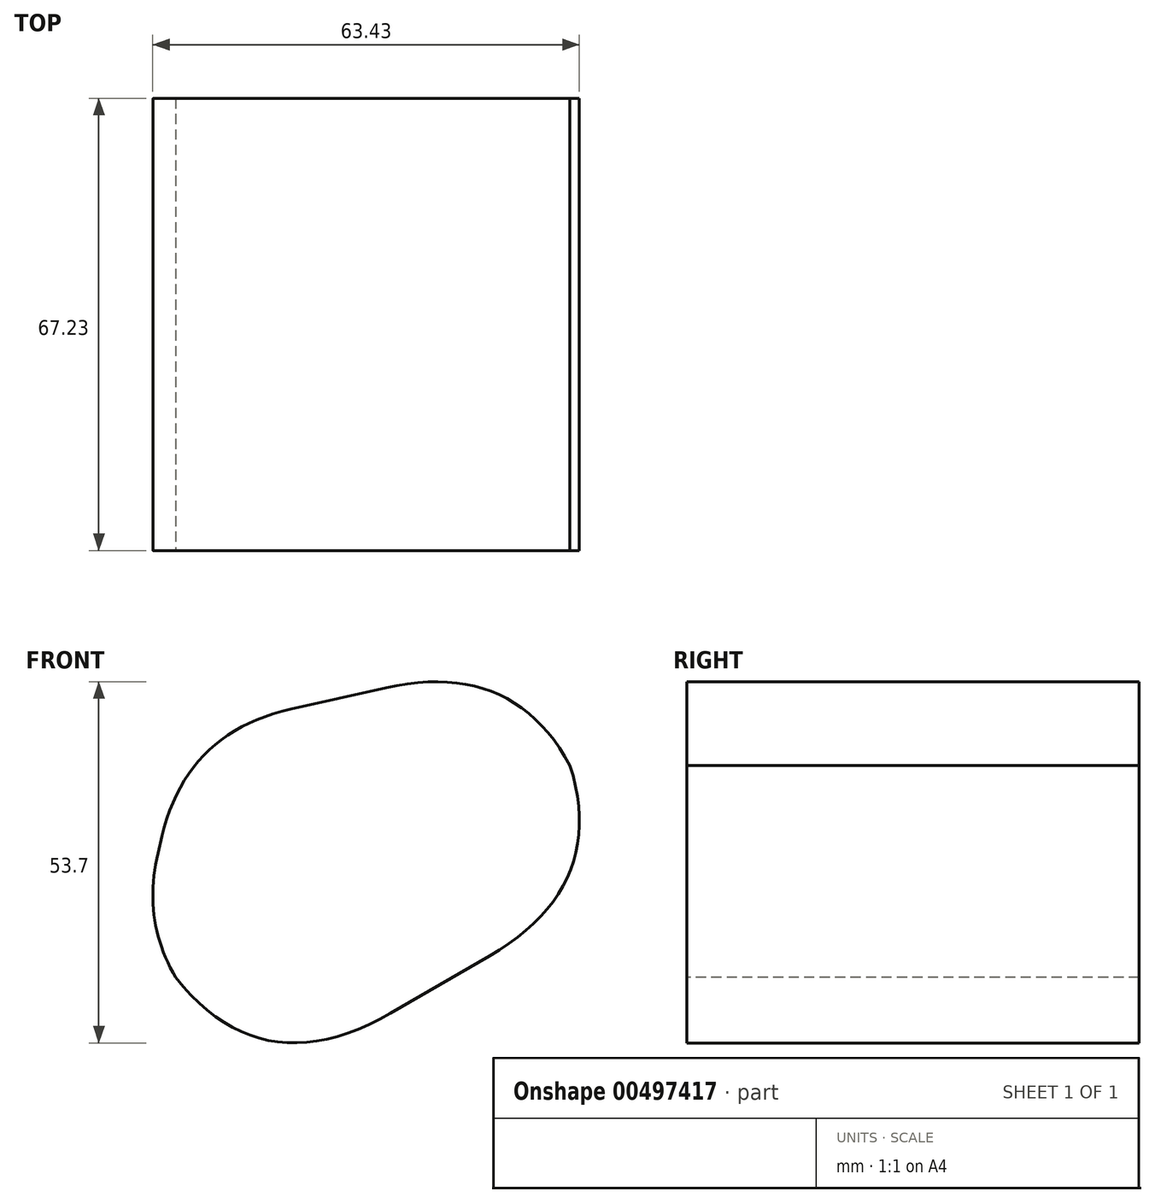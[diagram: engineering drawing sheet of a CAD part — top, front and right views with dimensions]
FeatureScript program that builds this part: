
annotation { "Feature Type Name" : "Feature", "Feature Type Description" : "" }
export const myFeature = defineFeature(function(context is Context, id is Id, definition is map)
    precondition{}
    {
        {
            var Q0;
            Q0=qCreatedBy(makeId("Front.planeOp"),FACE);
            var sketch = newSketch(context, id + "F0", { "sketchPlane" : qUnion([Q0])});
            skLineSegment(sketch, "E0", {"start": v(40.58, 6.97) * mm, "end": v(26.51, 40.26) * mm});
            skLineSegment(sketch, "E1", {"start": v(26.51, 40.26) * mm, "end": v(-23.82, 28.96) * mm});
            skLineSegment(sketch, "E2", {"start": v(-23.82, 28.96) * mm, "end": v(-30.74, 0) * mm});
            skLineSegment(sketch, "E3", {"start": v(-30.74, 0) * mm, "end": v(-13.74, -24.47) * mm});
            skLineSegment(sketch, "E4", {"start": v(-13.74, -24.47) * mm, "end": v(40.58, 6.97) * mm});
            skSolve(sketch);
        }
        {
            var Q0;
            Q0=makeQuery(id+"F0.imprint","IMPRINT",FACE,{"disambiguationData":[TD([[makeQuery(id+"F0.imprint","IMPRINT",EDGE,{"derivedFrom":sQuery(id+"F0.wireOp",EDGE,"E0")}),1.0]])]});
            extrude(context, id + "F1", {"entities" : qUnion([Q0]), "depth" : 67.23 * mm});
        }
        {
            var Q0;
            Q0=makeQuery(id+"F1.opExtrude","SWEPT_EDGE",EDGE,{"disambiguationData":[OSD([sQuery(id+"F0.wireOp",EDGE,"E0"),sQuery(id+"F0.wireOp",EDGE,"E1")])]});
            var Q1;
            Q1=makeQuery(id+"F1.opExtrude","SWEPT_EDGE",EDGE,{"disambiguationData":[OSD([sQuery(id+"F0.wireOp",EDGE,"E1"),sQuery(id+"F0.wireOp",EDGE,"E2")])]});
            var Q2;
            Q2=makeQuery(id+"F1.opExtrude","SWEPT_EDGE",EDGE,{"disambiguationData":[OSD([sQuery(id+"F0.wireOp",EDGE,"E0"),sQuery(id+"F0.wireOp",EDGE,"E4")])]});
            var Q3;
            Q3=makeQuery(id+"F1.opExtrude","SWEPT_EDGE",EDGE,{"disambiguationData":[OSD([sQuery(id+"F0.wireOp",EDGE,"E3"),sQuery(id+"F0.wireOp",EDGE,"E4")])]});
            var Q4;
            Q4=makeQuery(id+"F1.opExtrude","SWEPT_EDGE",EDGE,{"disambiguationData":[OSD([sQuery(id+"F0.wireOp",EDGE,"E2"),sQuery(id+"F0.wireOp",EDGE,"E3")])]});
            fillet(context, id + "F2", {"entities" : qUnion([Q0, Q1, Q2, Q3, Q4]), "radius" : 25.4 * mm, "tangentPropagation" : true, "rho" : 0.5, "crossSection" : FilletCrossSection.CONIC, "allowEdgeOverflow" : false});
        }
        {
            var Q0;
            Q0=makeQuery(id+"F1.opExtrude","CAP_FACE",FACE,{"disambiguationData":[OSD([sQuery(id+"F0.wireOp",EDGE,"E0"),sQuery(id+"F0.wireOp",EDGE,"E1"),sQuery(id+"F0.wireOp",EDGE,"E2"),sQuery(id+"F0.wireOp",EDGE,"E3"),sQuery(id+"F0.wireOp",EDGE,"E4")])],"isStart":false});
            var sketch = newSketch(context, id + "F3", { "sketchPlane" : qUnion([Q0])});
            skCircle(sketch, "E5", {"center": v(19.2, 16.68) * mm, "radius": 10.04 * mm});
            skSolve(sketch);
        }
        {
            var Q0;
            Q0=qCreatedBy(makeId("Top.planeOp"),FACE);
            var sketch = newSketch(context, id + "F4", { "sketchPlane" : qUnion([Q0])});
            skLineSegment(sketch, "E6", {"start": v(24.1, -67.25) * mm, "end": v(9.4, -85.1) * mm});
            skLineSegment(sketch, "E7", {"start": v(9.4, -85.1) * mm, "end": v(-27.06, -88.42) * mm});
            skSolve(sketch);
        }
    });
